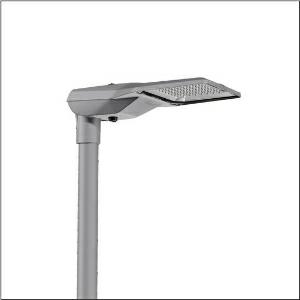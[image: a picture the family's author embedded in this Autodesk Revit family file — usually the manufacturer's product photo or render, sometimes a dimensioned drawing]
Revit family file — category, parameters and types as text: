
# Revit family: streetlight_sl_21_iq_midi___stw1_0a_5xe3e31y08mb_1dd4
name_source: partatom
category: Lighting Fixtures
units: mm (PartAtom-declared; Revit-internal decimal feet)

## family parameters
Cut with Voids When Loaded = No
Host = Face
Light Source = No
Part Type = Normal
Room Calculation Point = No
Round Connector Dimension = Use Diameter
Shared = No

## types (1)
- --- (1 x LED, 18340 lm, 129.3 W, 3000K)
    Apparent Load = 129 VA
    CIE Flux Codes = 38 75 98 100 100
    Color Rendering = 70
    Color Temperature = 3000K
    Default Elevation = 1800 mm
    Description = Streetlight SL 21 iQ midi, mast luminaire, primary light control with lens, of PMMA, primary optical cover: cover, of toughened safety glass, transparent, light distribution: STW1.0a, light emission: direct distribution, primary light characteristic: asymmetric, installation type: post-top, side-entry, LED, High Power LED, rated luminous flux: 18.340lm, luminous efficacy: 142lm/W, light colour: 730, colour temperature: 3000K, control gear: iQ-Street Remote, D4i with power reduction, control: pre-setting: logarithmic dimming characteristic, Street-Remote, Auto-Match, Temp-Guard, Lumen-Switch, Night-Set, Smart-Wire, Light-Fading, Desk-Remote (wireless, voltage-free reading and setting of iQ features in the workshop via application-optimized NFC function/RFID function), optimised constant luminous flux control (CLO 2.0), mains connection: 230..240V, AC, 50/60Hz, start of lifetime: 129W, end of service life: 142W, reduction: 56W, luminaire housing, of diecast aluminium, powder-coated, Siteco® metallic grey (DB 702S), corrosivity category C5 mid according to DIN EN ISO 12944, please order mast flange separately, inclination adjustable: 0°, 5°, 10°, 15°, sealing non-destructively replaceable, multi-level sealing system, length: 644mm, width: 335mm, height: 110mm, mast flange for spigot size: 42mm (side-entry): 5XC10008XM4, 60/48mm (side-entry/post-top): 5XC10108XM2, 76/60mm (side-entry/post-top): 5XC10108XM1, mounting height: 4..8m, Smart Interface below and above, protection rating (complete): IP66, insulation class (complete): insulation class II (safety insulation), certification: CE, ENEC, ENEC+, VDE, impact resistance: IK10, permissible operating ambient temperature for outdoor applications: -40..+50°C, standard-compliant lighting for roads and squares, packaging unit: 1 piece

Light Distribution: STW1.0a
    Height = 111 mm
    Lamp = 1 x LED
    Lamp Light Flux = 18340 lm
    Lamp Power = 129.3 W
    Lamp count = 1
    Length = 644 mm
    Luminous efficacy = 142 lm/W
    Manufacturer = Siteco
    ModVariant = No
    Model = 5XE3E31Y08MB
    Number of Poles = 1
    OnlyDefault = Yes
    Power Factor = 1
    Product Name = Streetlight SL 21 iQ midi | STW1.0a
    Product group = mast luminaire | pylon top
    ProductGroupID = 6100
    Protection Class = Protection class II
    Protection Degree = IP 66
    RLX_Detail_Level = 1
    RLX_Emergency_Light_Flux = 0 lm
    RLX_Emergency_Type = 0
    RLX_Emergency_Type_DB = No
    RlxData = <blob elided: 90941 chars, md5=b1dd4447>
    Socket = socket
    Standby Power = 0 W
    System Light Flux = 18340 lm
    System Power = 129 W
    Type Comments = factory setting: luminous flux: 100 % | dim-lin: 254 | 672 mA
    Type Image = l_1004304.jpg
    URL = http://relux.com
    VarID = @adj_135739
    Voltage = 0 V
    Weight = 0.00 kg
    Width = 336 mm

## geometry (parser evidence)
native form markers: Blend x4, Sweep x10
no freeform markers — native parametric forms only
